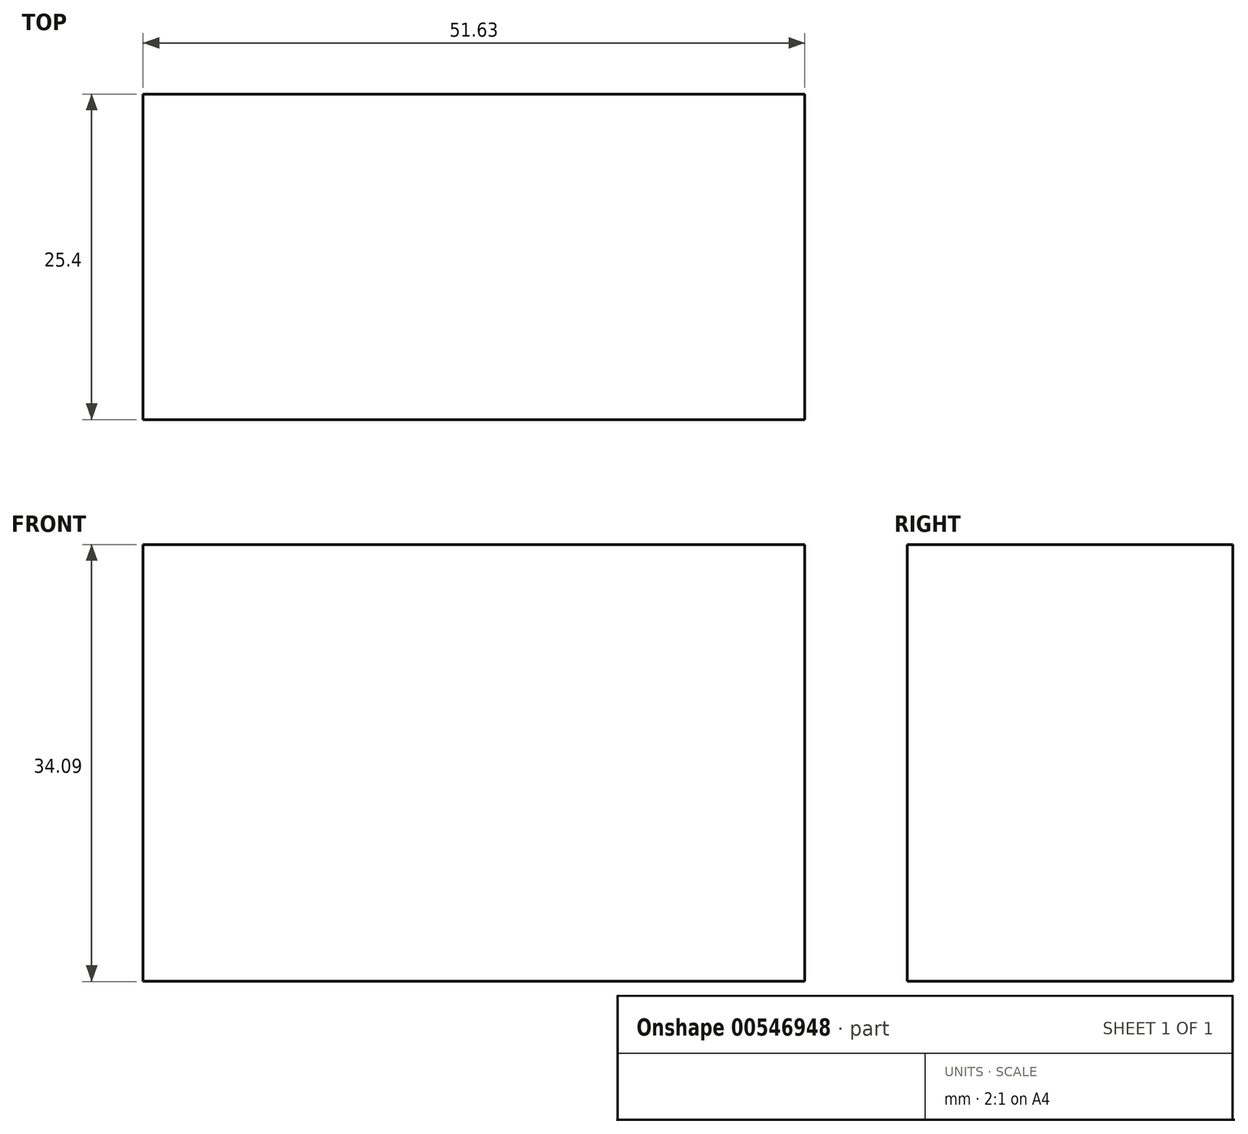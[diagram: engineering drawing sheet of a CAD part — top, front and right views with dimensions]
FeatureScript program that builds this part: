
annotation { "Feature Type Name" : "Feature", "Feature Type Description" : "" }
export const myFeature = defineFeature(function(context is Context, id is Id, definition is map)
    precondition{}
    {
        {
            var Q0;
            Q0=qCreatedBy(makeId("Front.planeOp"),FACE);
            var sketch = newSketch(context, id + "F0", { "sketchPlane" : qUnion([Q0])});
            skLineSegment(sketch, "E0.bottom", {"start": v(-54.2, 54.1) * mm, "end": v(-2.56, 54.1) * mm});
            skLineSegment(sketch, "E0.top", {"start": v(-54.2, 20.02) * mm, "end": v(-2.56, 20.02) * mm});
            skLineSegment(sketch, "E0.left", {"start": v(-54.2, 54.1) * mm, "end": v(-54.2, 20.02) * mm});
            skLineSegment(sketch, "E0.right", {"start": v(-2.56, 54.1) * mm, "end": v(-2.56, 20.02) * mm});
            skFitSpline(sketch, "E1", {"points": [v(22.32, -13.72) * mm, v(30.85, 14.91) * mm, v(59.65, 34.85) * mm, v(60.84, 7.92) * mm, v(31.19, -26.16) * mm, v(22.32, -13.72) * mm]});
            skSolve(sketch);
        }
        {
            var Q0;
            Q0 = qSketchRegion(id + "F0", true);
            extrude(context, id + "F1", {"entities" : qUnion([Q0]), "depth" : 25.4 * mm, "offsetDistance" : 25.4 * mm});
        }
        {
            var Q0;
            Q0=makeQuery(id+"F1.opExtrude","SWEPT_BODY",BODY,{"disambiguationData":[OSD([sQuery(id+"F0.wireOp",EDGE,"E1")])]});
            deleteBodies(context, id + "F2", {"entities" : qUnion([Q0])});
        }
        {
            var Q0;
            Q0=qCreatedBy(makeId("Front.planeOp"),FACE);
            var sketch = newSketch(context, id + "F3", { "sketchPlane" : qUnion([Q0])});
            skFitSpline(sketch, "E2", {"points": [v(-70.48, -56.56) * mm, v(-60.85, -43.66) * mm, v(-23.44, -61.3) * mm, v(-12.66, -47.98) * mm, v(-12.47, -48) * mm], "startDerivative": vector(22.7, 75.45) * mm, "endDerivative": vector(5.62, -4.62) * mm});
            skSolve(sketch);
        }
        {
            var Q0;
            Q0=sQuery(id+"F3.wireOp",EDGE,"E2");
            extrude(context, id + "F4", {"bodyType" : ToolBodyType.SURFACE, "surfaceEntities" : qUnion([Q0]), "endBound" : BoundingType.SYMMETRIC, "depth" : 68.58 * mm, "offsetDistance" : 25.4 * mm});
        }
    });
